# Revit family: Haworth_BuzziVille Hub
name_source: partatom
category: Furniture
revit_build: Autodesk Revit 2018 (Build: 20170223_1515(x64)
units: mm (PartAtom-declared; Revit-internal decimal feet)

## family parameters
Always vertical = Yes
Cut with Voids When Loaded = No
OmniClass Number = 23.40.70.14.64.21
OmniClass Title = Systems Furniture
Room Calculation Point = No
Shared = No
Work Plane-Based = No

## types (6) — shared parameters
Assembly Code = E2020200
Manufacturer = Haworth
Model = HCBZ-VLB
Revision Number = 1
Size = Verify Final Dim. w/ Haworth
URL = http://www.haworth.com
URL - Product = https://www.haworth.com
Warranty = http://www.haworth.com
zero-valued in all types: Actual Depth, Actual Height, Actual Width, Cushion Width, Front Height, Seat Width, Void Length

## per-type parameters (varying)
| type | Closed | Description | Large | Medium | Open | Small |
| HCBZ-VLB2-CF | Yes | Haworth BuzziVille Hub - Closed Booth - Medium | No | Yes | No | No |
| HCBZ-VLB1-CF | Yes | Haworth BuzziVille Hub - Closed Booth - Small | No | No | No | Yes |
| HCBZ-VLB3-CF | Yes | Haworth BuzziVille Hub - Closed Booth - Large | Yes | No | No | No |
| HCBZ-VLB3-OF | No | Haworth BuzziVille Hub - Open Booth - Large | Yes | No | Yes | No |
| HCBZ-VLB2-OF | No | Haworth BuzziVille Hub - Open Booth - Medium | No | Yes | Yes | No |
| HCBZ-VLB1-OF | No | Haworth BuzziVille Hub - Open Booth - Small | No | No | Yes | Yes |

## geometry (parser evidence)
native form markers: Sweep x5
no freeform markers — native parametric forms only
